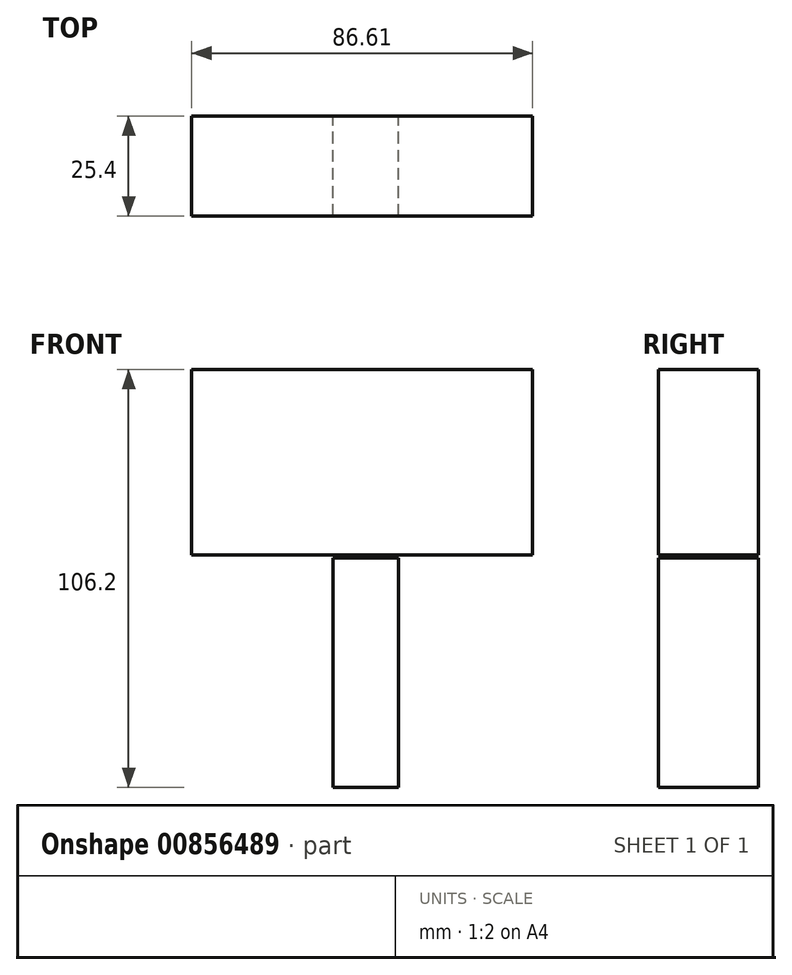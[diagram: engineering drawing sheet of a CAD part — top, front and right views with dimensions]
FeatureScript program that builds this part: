
annotation { "Feature Type Name" : "Feature", "Feature Type Description" : "" }
export const myFeature = defineFeature(function(context is Context, id is Id, definition is map)
    precondition{}
    {
        {
            var Q0;
            Q0=qCreatedBy(makeId("Front.planeOp"),FACE);
            var sketch = newSketch(context, id + "F0", { "sketchPlane" : qUnion([Q0])});
            skLineSegment(sketch, "E0.bottom", {"start": v(-34, 11.18) * mm, "end": v(-17.28, 11.18) * mm});
            skLineSegment(sketch, "E0.top", {"start": v(-34, -47.1) * mm, "end": v(-17.28, -47.1) * mm});
            skLineSegment(sketch, "E0.left", {"start": v(-34, 11.18) * mm, "end": v(-34, -47.1) * mm});
            skLineSegment(sketch, "E0.right", {"start": v(-17.28, 11.18) * mm, "end": v(-17.28, -47.1) * mm});
            skLineSegment(sketch, "E1.bottom", {"start": v(-69.88, 59.1) * mm, "end": v(16.73, 59.1) * mm});
            skLineSegment(sketch, "E1.top", {"start": v(-69.88, 11.92) * mm, "end": v(16.73, 11.92) * mm});
            skLineSegment(sketch, "E1.left", {"start": v(-69.88, 59.1) * mm, "end": v(-69.88, 11.92) * mm});
            skLineSegment(sketch, "E1.right", {"start": v(16.73, 59.1) * mm, "end": v(16.73, 11.92) * mm});
            skSolve(sketch);
        }
        {
            var Q0;
            Q0=makeQuery(id+"F0.imprint","IMPRINT",FACE,{"disambiguationData":[TD([[makeQuery(id+"F0.imprint","IMPRINT",EDGE,{"derivedFrom":sQuery(id+"F0.wireOp",EDGE,"E1.bottom")}),-1.0]])]});
            var Q1;
            Q1=makeQuery(id+"F0.imprint","IMPRINT",FACE,{"disambiguationData":[TD([[makeQuery(id+"F0.imprint","IMPRINT",EDGE,{"derivedFrom":sQuery(id+"F0.wireOp",EDGE,"E0.bottom")}),-1.0]])]});
            extrude(context, id + "F1", {"entities" : qUnion([Q0, Q1]), "depth" : 25.4 * mm, "offsetDistance" : 25.4 * mm});
        }
    });
